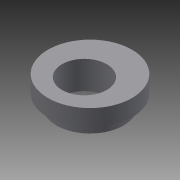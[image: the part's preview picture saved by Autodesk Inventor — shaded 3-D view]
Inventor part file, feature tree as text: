
AUTODESK INVENTOR PART (.ipt)
format: ipt  version: 2013 (Build 170138000, 138)  size: 87,040 bytes
history: native  units: mm
features: extrude x2, sketch x2
ambient origin geometry x8: Origin, YZ Plane, XZ Plane, XY Plane, X Axis, Y Axis, Z Axis, Center Point
bodies: Solid1 (feature_tree)
feature tree (4):
  extrude  "Extrusion1"  Depth=8.0mm
  extrude  "Extrusion2"  Depth=5.0mm TaperAngle=0.0deg
  sketch  "Sketch1"  dims[d0=12.0mm d1=8.0mm]
  sketch  "Sketch2"  dims[d2=1.0mm d3=5.0mm d4=0.0mm d5=15.0mm d6=3.0mm d7=0.0mm]
